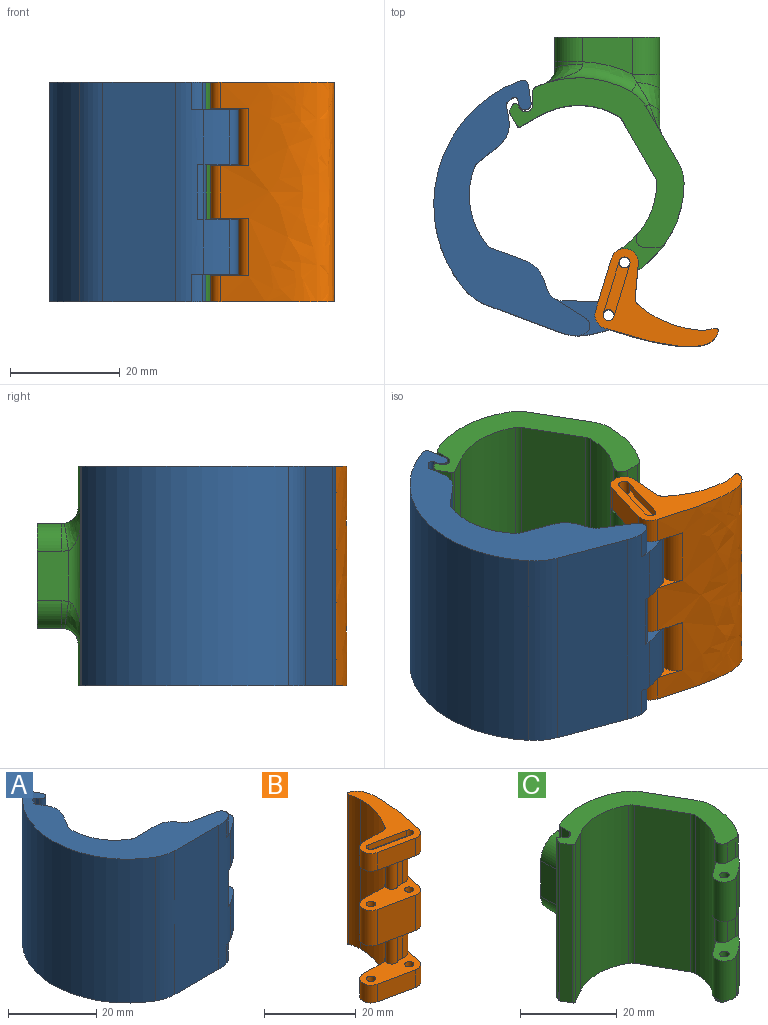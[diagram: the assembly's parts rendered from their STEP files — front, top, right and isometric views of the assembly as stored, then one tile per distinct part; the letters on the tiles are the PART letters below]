
ASSEMBLY  parts=3 mates=2
PART A: 46 faces, bbox 40.9x40.7x40 mm
  f0: plane 10x8mm, normal (-0.34,0.94,0), area 85mm2, adj f2,f4,f31,f33
  f1: plane 10x8mm, normal (-0.34,0.94,0), area 85mm2, adj f2,f14,f32,f35
  f2: cylinder r=2.76mm len=40mm, axis (0,0,1), area 100mm2, adj f0,f1,f5,f6,f15,f31,f32,f33
  f3: cylinder r=24.03mm len=10mm, axis (0,0,1), area 48.6mm2, adj f14,f30,f32,f35
  f4: cylinder r=2.5mm len=10mm, axis (0,0,1), area 68.8mm2, adj f0,f13,f31,f33
  f5: plane 40.65x35.95mm, normal (0,0,-1), area 424.6mm2, adj f2,f7,f8,f9,f10,f11,f12,f15
  f6: plane 40.65x35.95mm, normal (0,0,1), area 424.6mm2, adj f2,f7,f8,f9,f10,f11,f12,f15
  f7: plane 40x0.67mm, normal (-0.87,-0.5,0), area 31.2mm2, adj f5,f6,f8,f25
  f8: cylinder r=1.15mm len=40mm, axis (0,0,1), area 144.5mm2, adj f5,f6,f7,f9
  f9: plane 40x2.8mm, normal (0.87,0.5,0), area 129.1mm2, adj f5,f6,f8,f28
  f10: cylinder r=9.4mm len=40mm, axis (0,0,1), area 23.3mm2, adj f5,f6,f11,f28
  f11: cylinder r=24.03mm len=40mm, axis (0,0,1), area 1814.5mm2, adj f5,f6,f10,f29
  f12: plane 40x14.09mm, normal (0,-1,0), area 563.6mm2, adj f5,f6,f29,f30
  f13: cylinder r=24.03mm len=10mm, axis (0,0,1), area 48.6mm2, adj f4,f30,f31,f33
  f14: cylinder r=2.5mm len=10mm, axis (0,0,1), area 68.8mm2, adj f1,f3,f32,f35
  f15: plane 40x2.09mm, normal (0.74,0.67,0), area 112.7mm2, adj f2,f5,f6,f26
  f16: plane 40x6.72mm, normal (0,1,0), area 268.8mm2, adj f5,f6,f17,f26
  f17: cylinder r=2.1mm len=40mm, axis (0,0,1), area 44mm2, adj f5,f6,f16,f18
  f18: cylinder r=14.16mm len=40mm, axis (0,0,1), area 592.6mm2, adj f5,f6,f17,f19
  f19: cylinder r=2.1mm len=40mm, axis (0,0,1), area 44mm2, adj f5,f6,f18,f20
  f20: plane 40x4.4mm, normal (0.87,-0.5,0), area 203.3mm2, adj f5,f6,f19,f27
  f21: plane 40x2.3mm, normal (0.87,0.5,0), area 106.2mm2, adj f5,f6,f22,f27
  f22: cylinder r=0.6mm len=40mm, axis (0,0,1), area 25.1mm2, adj f5,f6,f21,f23
  f23: plane 40x0.7mm, normal (0.87,-0.5,0), area 32.3mm2, adj f5,f6,f22,f24
  f24: cylinder r=7.2mm len=40mm, axis (0,0,1), area 14.9mm2, adj f5,f6,f23,f25
  f25: cylinder r=0.6mm len=40mm, axis (0,0,1), area 49mm2, adj f5,f6,f7,f24
  f26: cylinder r=5mm len=40mm, axis (0,0,1), area 167.1mm2, adj f5,f6,f15,f16
  f27: cylinder r=5mm len=40mm, axis (0,0,1), area 209.4mm2, adj f5,f6,f20,f21
  f28: cylinder r=1mm len=40mm, axis (0,0,1), area 68.1mm2, adj f5,f6,f9,f10
  f29: cylinder r=10mm len=40mm, axis (0,0,1), area 210.4mm2, adj f5,f6,f11,f12
  f30: cylinder r=10mm len=40mm, axis (0,0,1), area 175.5mm2, adj f3,f5,f6,f12,f13,f31,f32,f33
  f31: plane 12.85x8.11mm, normal (0,0,-1), area 37.7mm2, adj f0,f2,f4,f13,f30,f36,f38,f42
  f32: plane 12.85x7.75mm, normal (0,0,-1), area 37.3mm2, adj f1,f2,f3,f14,f30,f34,f37,f41
  f33: plane 12.85x7.75mm, normal (0,0,1), area 37.3mm2, adj f0,f2,f4,f13,f30,f36,f37,f41
  f34: cylinder r=1mm len=10mm, axis (0,0,1), area 62.8mm2, adj f32,f35
  f35: plane 12.85x8.11mm, normal (0,0,1), area 37.7mm2, adj f1,f2,f3,f14,f30,f34,f39,f40
  f36: cylinder r=1mm len=10mm, axis (0,0,1), area 62.8mm2, adj f31,f33
  f37: cylinder r=3.1mm len=10mm, axis (0,0,1), area 12.8mm2, adj f30,f32,f33,f44
  f38: cylinder r=3.1mm len=5mm, axis (0,0,1), area 10.6mm2, adj f5,f30,f31,f43
  f39: cylinder r=3.1mm len=5mm, axis (0,0,1), area 10.6mm2, adj f6,f30,f35,f45
  f40: plane 6.76x5mm, normal (0.21,0.98,0), area 34.5mm2, adj f2,f6,f35,f45
  f41: plane 10x6.87mm, normal (0.21,0.98,0), area 70.2mm2, adj f2,f32,f33,f44
  f42: plane 6.76x5mm, normal (0.21,0.98,0), area 34.5mm2, adj f2,f5,f31,f43
  f43: cylinder r=1.5mm len=5mm, axis (0,0,1), area 14.6mm2, adj f5,f31,f38,f42
  f44: cylinder r=1.5mm len=10mm, axis (0,0,1), area 28.4mm2, adj f32,f33,f37,f41
  f45: cylinder r=1.5mm len=5mm, axis (0,0,1), area 14.6mm2, adj f6,f35,f39,f40
PART B: 45 faces, bbox 18.8x23.6x40 mm
  f0: plane 23.62x18.83mm, normal (0,0,-1), area 124.3mm2, adj f1,f4,f6,f7,f10,f14,f16,f19
  f1: cylinder r=2.5mm len=4.74mm, axis (0,0,1), area 18.9mm2, adj f0,f6,f7,f22
  f2: cylinder r=2.5mm len=9.47mm, axis (0,0,1), area 37.9mm2, adj f6,f9,f20,f21
  f3: cylinder r=2.5mm len=4.74mm, axis (0,0,1), area 18.9mm2, adj f6,f8,f12,f23
  f4: cylinder r=1mm len=4.74mm, axis (0,0,1), area 25.1mm2, adj f0,f22,f42,f43,f44
  f5: cylinder r=1mm len=4.74mm, axis (0,0,1), area 25.1mm2, adj f12,f23,f39,f40,f41
  f6: extruded ~40x20.56mm, area 778.9mm2, adj f0,f1,f2,f3,f12,f20,f21,f22
  f7: plane 9.79x4.74mm, normal (-0.21,-0.98,0), area 47.4mm2, adj f0,f1,f16,f22
  f8: plane 9.79x4.74mm, normal (-0.21,-0.98,0), area 47.4mm2, adj f3,f12,f15,f23
  f9: plane 9.79x9.48mm, normal (-0.21,-0.98,0), area 94.7mm2, adj f2,f17,f20,f21
  f10: cylinder r=19.42mm len=40mm, axis (0,0,-1), area 498.5mm2, adj f0,f12,f20,f21,f22,f23,f24,f33
  f11: plane 9.48x6.24mm, normal (0,1,0), area 59.2mm2, adj f17,f20,f21,f36
  f12: plane 23.62x18.83mm, normal (0,0,1), area 124.3mm2, adj f3,f5,f6,f8,f10,f13,f15,f18
  f13: cylinder r=1mm len=4.74mm, axis (0,0,1), area 25.1mm2, adj f12,f23,f39,f40,f41
  f14: cylinder r=1mm len=4.74mm, axis (0,0,1), area 25.1mm2, adj f0,f22,f42,f43,f44
  f15: cylinder r=2.5mm len=4.95mm, axis (0,0,1), area 34.7mm2, adj f8,f12,f18,f23
  f16: cylinder r=2.5mm len=4.95mm, axis (0,0,1), area 34.7mm2, adj f0,f7,f19,f22
  f17: cylinder r=2.5mm len=9.47mm, axis (0,0,1), area 69.5mm2, adj f9,f11,f20,f21
  f18: plane 6.24x4.74mm, normal (0,1,0), area 29.6mm2, adj f12,f15,f23,f37
  f19: plane 6.24x4.74mm, normal (0,1,0), area 29.6mm2, adj f0,f16,f22,f38
  f20: plane 15.87x7.69mm, normal (0,0,1), area 70.7mm2, adj f2,f6,f9,f10,f11,f17,f25,f26
  f21: plane 15.87x7.69mm, normal (0,0,-1), area 70.7mm2, adj f2,f6,f9,f10,f11,f17,f25,f28
  f22: plane 15.87x7.69mm, normal (0,0,1), area 70.7mm2, adj f1,f4,f6,f7,f10,f14,f16,f19
  f23: plane 15.87x7.69mm, normal (0,0,-1), area 70.7mm2, adj f3,f5,f6,f8,f10,f13,f15,f18
  f24: cylinder r=7.36mm len=40mm, axis (0,0,-1), area 120.7mm2, adj f0,f10,f12,f35
  f25: cylinder r=1mm len=9.47mm, axis (0,0,1), area 59.5mm2, adj f20,f21
  f26: plane 10.53x0.34mm, normal (0.34,-0.94,0), area 3.8mm2, adj f20,f23,f27,f34
  f27: cylinder r=2.76mm len=10.53mm, axis (0,0,1), area 16.1mm2, adj f20,f23,f26,f32
  f28: plane 10.53x0.34mm, normal (0.34,-0.94,0), area 3.8mm2, adj f21,f22,f29,f33
  f29: cylinder r=2.76mm len=10.53mm, axis (0,0,1), area 16.1mm2, adj f21,f22,f28,f31
  f30: cylinder r=1mm len=9.47mm, axis (0,0,1), area 59.5mm2, adj f20,f21
  f31: cylinder r=2.5mm len=10.53mm, axis (0,0,1), area 42mm2, adj f6,f21,f22,f29
  f32: cylinder r=2.5mm len=10.53mm, axis (0,0,1), area 42mm2, adj f6,f20,f23,f27
  f33: cylinder r=1.34mm len=10.53mm, axis (0,0,-1), area 36.4mm2, adj f10,f21,f22,f28
  f34: cylinder r=1.34mm len=10.53mm, axis (0,0,-1), area 36.4mm2, adj f10,f20,f23,f26
  f35: cylinder r=0.5mm len=40mm, axis (0,0,1), area 41.7mm2, adj f0,f6,f12,f24
  f36: cylinder r=1.5mm len=9.48mm, axis (0,0,-1), area 13.5mm2, adj f10,f11,f20,f21
  f37: cylinder r=1.5mm len=4.74mm, axis (0,0,-1), area 6.8mm2, adj f10,f12,f18,f23
  f38: cylinder r=1.5mm len=4.74mm, axis (0,0,-1), area 6.8mm2, adj f0,f10,f19,f22
  f39: plane 10.2x4.02mm, normal (0,0,1), area 16.9mm2, adj f5,f13,f40,f41
  f40: plane 9.79x2.06mm, normal (0.21,0.98,0), area 15mm2, adj f5,f12,f13,f39
  f41: plane 9.79x2.06mm, normal (-0.21,-0.98,0), area 15mm2, adj f5,f12,f13,f39
  f42: plane 10.2x4.02mm, normal (0,0,-1), area 16.9mm2, adj f4,f14,f43,f44
  f43: plane 9.79x2.06mm, normal (0.21,0.98,0), area 15mm2, adj f0,f4,f14,f42
  f44: plane 9.79x2.06mm, normal (-0.21,-0.98,0), area 15mm2, adj f0,f4,f14,f42
PART C: 70 faces, bbox 31.9x43.6x40.1 mm
  f0: cylinder r=7.1mm len=7.54mm, axis (0,0,-1), area 28mm2, adj f1,f9,f11,f50
  f1: plane 31.8x30.82mm, normal (0,0,-1), area 244.9mm2, adj f0,f2,f3,f6,f7,f8,f9,f11
  f2: cylinder r=19.16mm len=40mm, axis (0,0,-1), area 635.7mm2, adj f1,f4,f5,f8,f21,f22,f23,f25
  f3: cylinder r=14.16mm len=40mm, axis (0,0,-1), area 496.2mm2, adj f1,f4,f5,f7,f21,f22,f23,f25
  f4: cylinder r=2.5mm len=10mm, axis (0,0,-1), area 78.6mm2, adj f2,f3,f22,f26
  f5: cylinder r=2.5mm len=10mm, axis (0,0,-1), area 78.6mm2, adj f2,f3,f23,f25
  f6: plane 40x10.45mm, normal (-0.87,-0.5,0), area 482.7mm2, adj f1,f7,f20,f21
  f7: cylinder r=2.1mm len=40mm, axis (0,0,-1), area 44mm2, adj f1,f3,f6,f21
  f8: cylinder r=7.1mm len=40mm, axis (0,0,-1), area 148.8mm2, adj f1,f2,f9,f21
  f9: plane 40x10.45mm, normal (0.87,0.5,0), area 336.1mm2, adj f0,f1,f8,f10,f21,f46,f47,f48
  f10: cylinder r=7.1mm len=7.54mm, axis (0,0,-1), area 28mm2, adj f9,f11,f21,f49
  f11: cylinder r=19.16mm len=40mm, axis (0,0,-1), area 313mm2, adj f0,f1,f10,f21,f31,f51,f52,f53
  f12: plane 40x2.34mm, normal (-1,0,0), area 93.7mm2, adj f1,f13,f21,f31
  f13: cylinder r=1.25mm len=40mm, axis (0,0,-1), area 130.9mm2, adj f1,f12,f14,f21
  f14: plane 40x0.67mm, normal (0.87,0.5,0), area 31.2mm2, adj f1,f13,f21,f28
  f15: cylinder r=7.1mm len=40mm, axis (0,0,-1), area 14.7mm2, adj f1,f16,f21,f28
  f16: plane 40x0.7mm, normal (-0.87,0.5,0), area 32.3mm2, adj f1,f15,f21,f29
  f17: plane 40x2.35mm, normal (-0.87,-0.5,0), area 108.5mm2, adj f1,f21,f29,f30
  f18: plane 40x3.47mm, normal (0.5,-0.87,0), area 160mm2, adj f1,f19,f21,f30
  f19: cylinder r=14.16mm len=40mm, axis (0,0,-1), area 592.6mm2, adj f1,f18,f20,f21
  f20: cylinder r=2.1mm len=40mm, axis (0,0,-1), area 44mm2, adj f1,f6,f19,f21
  f21: plane 31.8x30.82mm, normal (0,0,1), area 244.9mm2, adj f2,f3,f6,f7,f8,f9,f10,f11
  f22: plane 9.84x7.74mm, normal (0,0,-1), area 31.9mm2, adj f2,f3,f4,f24,f33,f37,f38
  f23: plane 9.84x7.74mm, normal (0,0,1), area 31.9mm2, adj f2,f3,f5,f27,f33,f37,f38
  f24: cylinder r=1mm len=10mm, axis (0,0,-1), area 62.8mm2, adj f22,f26
  f25: plane 9.84x7.74mm, normal (0,0,-1), area 31.9mm2, adj f2,f3,f5,f27,f34,f35,f36
  f26: plane 9.84x7.74mm, normal (0,0,1), area 31.9mm2, adj f2,f3,f4,f24,f32,f39,f40
  f27: cylinder r=1mm len=10mm, axis (0,0,-1), area 62.8mm2, adj f23,f25
  f28: cylinder r=0.5mm len=40mm, axis (0,0,-1), area 40.9mm2, adj f1,f14,f15,f21
  f29: cylinder r=0.5mm len=40mm, axis (0,0,-1), area 20.9mm2, adj f1,f16,f17,f21
  f30: cylinder r=0.5mm len=40mm, axis (0,0,1), area 31.4mm2, adj f1,f17,f18,f21
  f31: cylinder r=1mm len=40mm, axis (0,0,-1), area 46mm2, adj f1,f11,f12,f21
  f32: plane 5x2.53mm, normal (0,-1,0), area 12.6mm2, adj f21,f26,f39,f40
  f33: plane 10x2.53mm, normal (0,-1,0), area 25.3mm2, adj f22,f23,f37,f38
  f34: plane 5x2.53mm, normal (0,-1,0), area 12.6mm2, adj f1,f25,f35,f36
  f35: cylinder r=1.5mm len=5mm, axis (0,0,-1), area 7.2mm2, adj f1,f2,f25,f34
  f36: cylinder r=1.5mm len=5mm, axis (0,0,-1), area 17.1mm2, adj f1,f3,f25,f34
  f37: cylinder r=1.5mm len=10mm, axis (0,0,-1), area 14.4mm2, adj f2,f22,f23,f33
  f38: cylinder r=1.5mm len=10mm, axis (0,0,-1), area 34.2mm2, adj f3,f22,f23,f33
  f39: cylinder r=1.5mm len=5mm, axis (0,0,-1), area 7.2mm2, adj f2,f21,f26,f32
  f40: cylinder r=1.5mm len=5mm, axis (0,0,-1), area 17.1mm2, adj f3,f21,f26,f32
  f41: plane 19.05x19.05mm, normal (0,1,0), area 341.4mm2, adj f42,f43,f44,f45,f54,f57,f62,f65
  f42: plane 9.24x5.73mm, normal (-1,0,0), area 51.9mm2, adj f41,f53,f54,f55,f62,f63
  f43: plane 17.07x16.3mm, normal (1,0,0), area 173.5mm2, adj f41,f46,f57,f58,f59,f60,f65,f66
  f44: plane 9.05x6.75mm, normal (0,0,1), area 47.8mm2, adj f41,f51,f62,f65
  f45: plane 9.05x6.75mm, normal (0,0,-1), area 47.8mm2, adj f41,f52,f54,f57
  f46: cylinder r=2.94mm len=24.93mm, axis (0,0,-1), area 32.3mm2, adj f9,f43,f61,f69
  f47: cylinder r=2.94mm len=5.5mm, axis (-0.5,0.87,0), area 6.7mm2, adj f9,f49,f68,f69
  f48: cylinder r=2.94mm len=5.5mm, axis (0.5,-0.87,0), area 6.7mm2, adj f9,f50,f60,f61
  f49: torus R=10.04mm, axis (0,0,1), area 11mm2, adj f10,f47,f51,f67
  f50: torus R=10.04mm, axis (0,0,1), area 11mm2, adj f0,f48,f52,f59
  f51: torus R=22.1mm, axis (0,0,1), area 55.2mm2, adj f11,f44,f49,f63,f64,f66
  f52: torus R=22.1mm, axis (0,0,1), area 55.2mm2, adj f11,f45,f50,f55,f56,f58
  f53: cylinder r=2.94mm len=24.93mm, axis (0,0,-1), area 55mm2, adj f11,f42,f56,f64
  f54: cylinder r=5mm len=5mm, axis (0,-1,0), area 35.4mm2, adj f41,f42,f45,f55
  f55: bspline ~5.26x5.07mm, area 5.8mm2, adj f42,f52,f54,f56
  f56: bspline ~7.95x7.01mm, area 27.1mm2, adj f52,f53,f55
  f57: cylinder r=5mm len=6.75mm, axis (0,1,0), area 53mm2, adj f41,f43,f45,f58
  f58: bspline ~5.3x5.24mm, area 15.8mm2, adj f43,f52,f57,f59
  f59: bspline ~6.46x5.7mm, area 24.4mm2, adj f43,f50,f58,f60
  f60: bspline ~4.03x3.98mm, area 9mm2, adj f43,f48,f59,f61
  f61: bspline ~3.97x3.64mm, area 6.8mm2, adj f46,f48,f60
  f62: cylinder r=5mm len=5mm, axis (0,1,0), area 35.4mm2, adj f41,f42,f44,f63
  f63: bspline ~5.26x5.07mm, area 5.8mm2, adj f42,f51,f62,f64
  f64: bspline ~7.95x7.01mm, area 27.1mm2, adj f51,f53,f63
  f65: cylinder r=5mm len=6.75mm, axis (0,-1,0), area 53mm2, adj f41,f43,f44,f66
  f66: bspline ~5.23x5.23mm, area 15.8mm2, adj f43,f51,f65,f67
  f67: bspline ~7.35x6mm, area 24.4mm2, adj f43,f49,f66,f68
  f68: bspline ~4.03x3.98mm, area 9mm2, adj f43,f47,f67,f69
  f69: bspline ~3.97x3.64mm, area 6.8mm2, adj f46,f47,f68
PLACE A rot(axis=(0,0,-1),20.5deg) t=(-5.76,-2.2,0)mm
PLACE B rot(axis=(0,0,-1),95deg) t=(23.43,-7.38,0)mm
PLACE C at identity fixed
MATE cylindrical C.f4 <-> B.f13  axis (0,0,1) through (8.33,-14.42,15)mm
MATE cylindrical A.f4 <-> B.f1  axis (0,0,1) through (5.43,-23.99,15)mm
